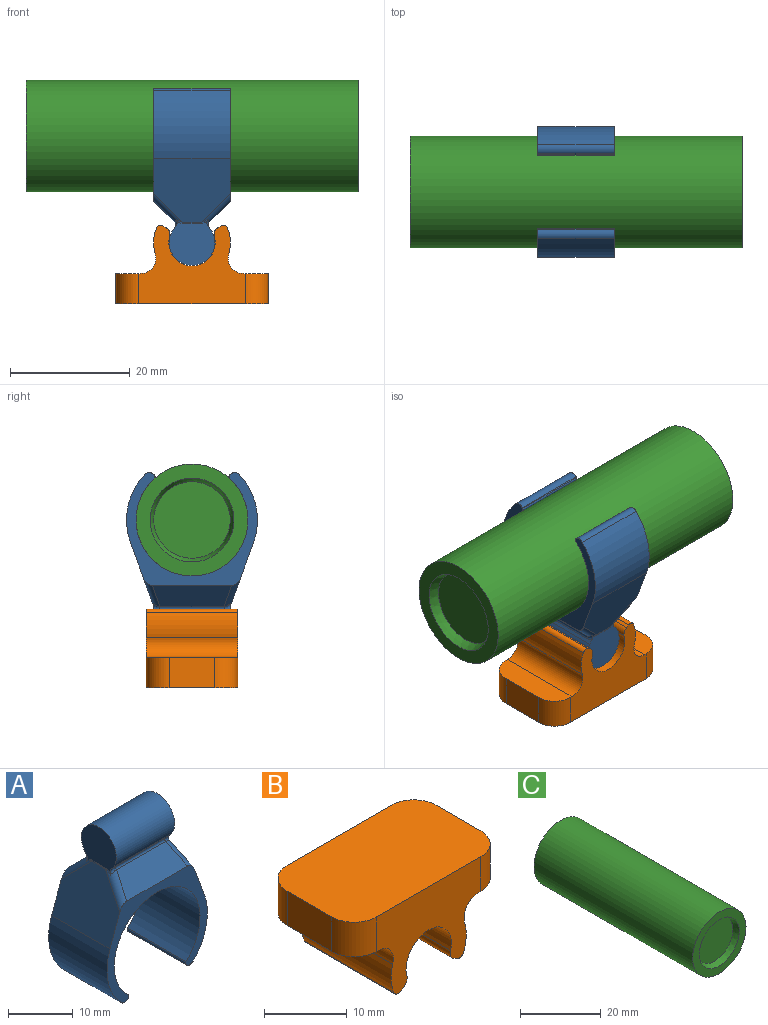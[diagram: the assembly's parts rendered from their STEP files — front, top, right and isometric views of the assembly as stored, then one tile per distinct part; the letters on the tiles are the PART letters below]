
ASSEMBLY  parts=3 mates=2
PART A: 36 faces, bbox 22.2x14.9x29.9 mm
  f0: plane 12.7x0.11mm, normal (0.77,0,-0.64), area 1.9mm2, adj f7,f8,f9,f16
  f1: plane 12.7x0.11mm, normal (-0.77,0,-0.64), area 1.9mm2, adj f2,f8,f9,f17
  f2: cylinder r=1.02mm len=12.7mm, axis (0,1,0), area 21.6mm2, adj f1,f3,f8,f9
  f3: cylinder r=10.92mm len=12.7mm, axis (0,1,0), area 155.2mm2, adj f2,f4,f8,f9
  f4: plane 12.7x10.67mm, normal (0.94,0,0.34), area 119.2mm2, adj f3,f8,f9,f22,f23,f34
  f5: plane 12.7x10.67mm, normal (-0.94,0,0.34), area 119.2mm2, adj f6,f8,f9,f20,f21,f25
  f6: cylinder r=10.92mm len=12.7mm, axis (0,1,0), area 155.2mm2, adj f5,f7,f8,f9
  f7: cylinder r=1.02mm len=12.7mm, axis (0,1,0), area 21.6mm2, adj f0,f6,f8,f9
  f8: plane 22.2x19.19mm, normal (0,-1,0), area 98.8mm2, adj f0,f1,f2,f3,f4,f5,f6,f7
  f9: plane 22.2x19.19mm, normal (0,1,0), area 98.8mm2, adj f0,f1,f2,f3,f4,f5,f6,f7
  f10: cylinder r=3.81mm len=12.7mm, axis (-1,0,0), area 211.1mm2, adj f11,f12,f13,f14
  f11: plane 12.7x0.74mm, normal (0,-0.82,-0.57), area 7.9mm2, adj f10,f13,f14,f29,f31,f33
  f12: plane 12.7x0.74mm, normal (0,0.82,-0.57), area 7.9mm2, adj f10,f13,f14,f26,f28,f30
  f13: plane 7.67x7.32mm, normal (1,0,0), area 44.3mm2, adj f10,f11,f12,f30,f32,f33,f34,f35
  f14: plane 7.67x7.32mm, normal (-1,0,0), area 44.3mm2, adj f10,f11,f12,f24,f25,f26,f27,f29
  f15: cylinder r=9.33mm len=18.67mm, axis (0,-1,0), area 570mm2, adj f8,f9,f16,f17
  f16: cylinder r=0.38mm len=12.7mm, axis (0,-1,0), area 7.4mm2, adj f0,f8,f9,f15
  f17: cylinder r=0.38mm len=12.7mm, axis (0,-1,0), area 7.4mm2, adj f1,f8,f9,f15
  f18: plane 13.25x3.52mm, normal (0,0.71,0.71), area 59.6mm2, adj f9,f20,f22,f28
  f19: plane 13.25x3.52mm, normal (0,-0.71,0.71), area 59.6mm2, adj f8,f21,f23,f31
  f20: cylinder r=1.27mm len=5.74mm, axis (-0.25,0.68,-0.68), area 9.5mm2, adj f5,f9,f18,f24,f26
  f21: cylinder r=1.27mm len=5.74mm, axis (-0.25,-0.68,-0.68), area 9.5mm2, adj f5,f8,f19,f27,f29
  f22: cylinder r=1.27mm len=5.74mm, axis (-0.25,-0.68,0.68), area 9.5mm2, adj f4,f9,f18,f30,f32
  f23: cylinder r=1.27mm len=5.74mm, axis (-0.25,0.68,0.68), area 9.5mm2, adj f4,f8,f19,f33,f35
  f24: bspline ~2.02x1.01mm, area 0.3mm2, adj f14,f20,f25,f26
  f25: cylinder r=0.51mm len=3.01mm, axis (0,1,0), area 0.5mm2, adj f5,f14,f24,f27
  f26: bspline ~1.52x1.18mm, area 0.9mm2, adj f12,f14,f20,f24,f28
  f27: bspline ~2.02x1.01mm, area 0.3mm2, adj f14,f21,f25,f29
  f28: cylinder r=0.51mm len=10.68mm, axis (1,0,0), area 7.6mm2, adj f12,f18,f26,f30
  f29: bspline ~1.52x1.18mm, area 0.9mm2, adj f11,f14,f21,f27,f31
  f30: bspline ~1.52x1.18mm, area 0.9mm2, adj f12,f13,f22,f28,f32
  f31: cylinder r=0.51mm len=10.68mm, axis (1,0,0), area 7.6mm2, adj f11,f19,f29,f33
  f32: bspline ~2.02x1.01mm, area 0.3mm2, adj f13,f22,f30,f34
  f33: bspline ~1.52x1.18mm, area 0.9mm2, adj f11,f13,f23,f31,f35
  f34: cylinder r=0.51mm len=3.01mm, axis (0,-1,0), area 0.5mm2, adj f4,f13,f32,f35
  f35: bspline ~2.02x1.01mm, area 0.3mm2, adj f13,f23,f33,f34
PART B: 22 faces, bbox 25.4x15.2x13.1 mm
  f0: plane 7.62x5.08mm, normal (1,0,0), area 38.7mm2, adj f1,f9,f19,f21
  f1: plane 25.4x15.24mm, normal (0,0,1), area 374.6mm2, adj f0,f2,f10,f11,f18,f19,f20,f21
  f2: plane 7.62x5.08mm, normal (-1,0,0), area 38.7mm2, adj f1,f3,f18,f20
  f3: plane 15.24x4.14mm, normal (0,0,-1), area 56.8mm2, adj f2,f10,f11,f12,f18,f20
  f4: cylinder r=6.41mm len=15.24mm, axis (0,1,0), area 67mm2, adj f10,f11,f12,f16
  f5: plane 15.24x0.53mm, normal (0.5,0,-0.87), area 9.4mm2, adj f10,f11,f14,f16
  f6: cylinder r=3.87mm len=15.24mm, axis (0,1,0), area 217.8mm2, adj f10,f11,f14,f15
  f7: plane 15.24x0.53mm, normal (-0.5,0,-0.87), area 9.4mm2, adj f10,f11,f15,f17
  f8: cylinder r=6.41mm len=15.24mm, axis (0,1,0), area 67mm2, adj f10,f11,f13,f17
  f9: plane 15.24x4.14mm, normal (0,0,-1), area 56.8mm2, adj f0,f10,f11,f13,f19,f21
  f10: plane 17.78x13.14mm, normal (0,-1,0), area 145.8mm2, adj f1,f3,f4,f5,f6,f7,f8,f9
  f11: plane 17.78x13.14mm, normal (0,1,0), area 145.8mm2, adj f1,f3,f4,f5,f6,f7,f8,f9
  f12: cylinder r=2.54mm len=15.24mm, axis (0,1,0), area 72.3mm2, adj f3,f4,f10,f11
  f13: cylinder r=2.54mm len=15.24mm, axis (0,1,0), area 72.3mm2, adj f8,f9,f10,f11
  f14: cylinder r=1.27mm len=15.24mm, axis (0,1,0), area 25.6mm2, adj f5,f6,f10,f11
  f15: cylinder r=1.27mm len=15.24mm, axis (0,1,0), area 25.6mm2, adj f6,f7,f10,f11
  f16: cylinder r=0.76mm len=15.24mm, axis (0,1,0), area 19.8mm2, adj f4,f5,f10,f11
  f17: cylinder r=0.76mm len=15.24mm, axis (0,1,0), area 19.8mm2, adj f7,f8,f10,f11
  f18: cylinder r=3.81mm len=5.08mm, axis (0,0,-1), area 30.4mm2, adj f1,f2,f3,f11
  f19: cylinder r=3.81mm len=5.08mm, axis (0,0,1), area 30.4mm2, adj f0,f1,f9,f11
  f20: cylinder r=3.81mm len=5.08mm, axis (0,0,1), area 30.4mm2, adj f1,f2,f3,f10
  f21: cylinder r=3.81mm len=5.08mm, axis (0,0,-1), area 30.4mm2, adj f0,f1,f9,f10
PART C: 5 faces, bbox 18.7x55.4x18.7 mm
  f0: cylinder r=9.33mm len=55.37mm, axis (0,-1,0), area 3247.6mm2, adj f1,f2
  f1: plane 18.67x18.67mm, normal (0,1,0), area 273.7mm2, adj f0
  f2: plane 18.67x18.67mm, normal (0,-1,0), area 120.5mm2, adj f0,f3
  f3: cone r=6.99mm half-angle=20deg, axis (0,-1,0), area 73.8mm2, adj f2,f4
  f4: plane 12.77x12.77mm, normal (0,-1,0), area 128mm2, adj f3
PLACE A rot(axis=(0.71,-0.71,0),180deg) t=(0,0,28.02)mm
PLACE B rot(axis=(0,1,0),180deg) t=(0,0,10.24)mm
PLACE C rot(axis=(-0.7,-0.7,-0.18),159.4deg) t=(-27.69,0,28.02)mm
MATE revolute A.f15 <-> C.f0  axis (1,0,0) through (0,0,28.02)mm
MATE revolute B.f6 <-> A.f10  axis (0,1,0) through (0,0,10.24)mm
